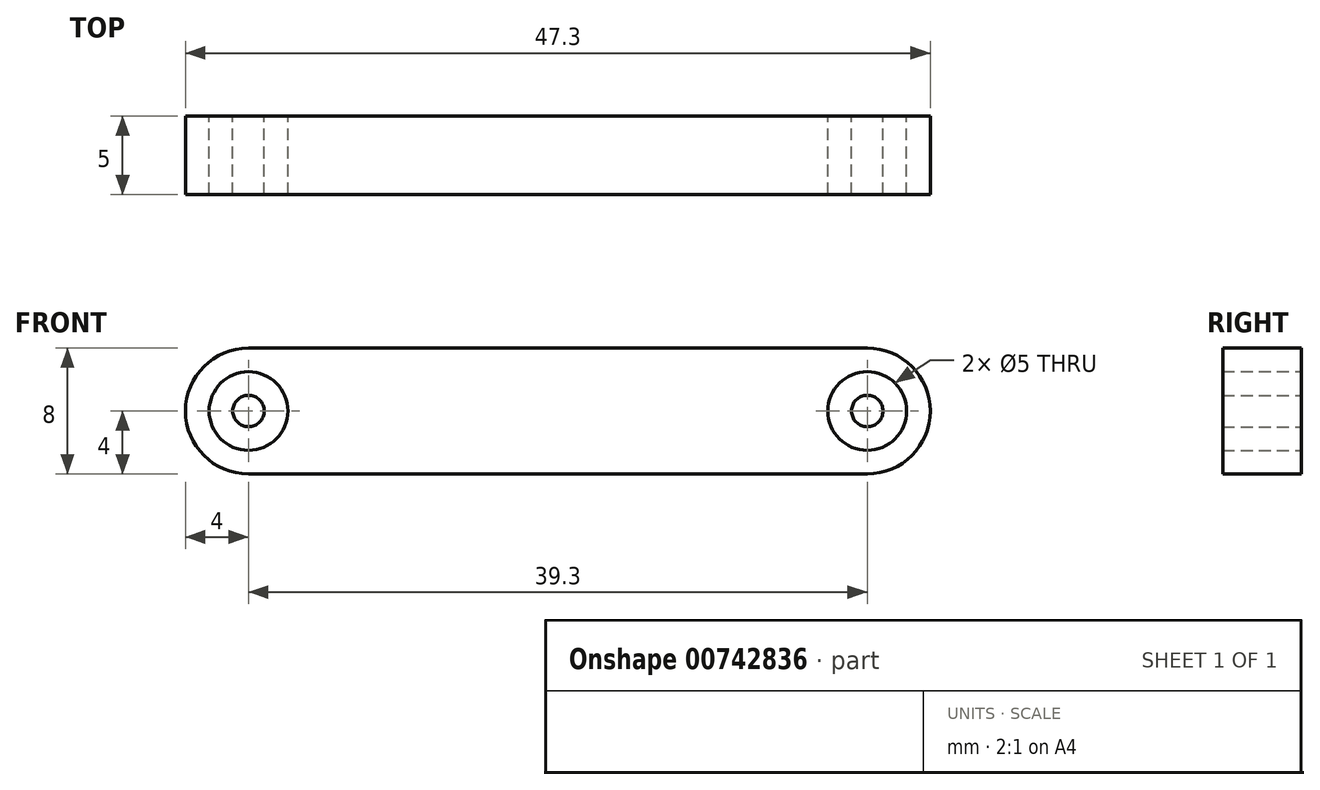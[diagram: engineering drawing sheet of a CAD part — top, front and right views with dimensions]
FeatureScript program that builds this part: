
annotation { "Feature Type Name" : "Feature", "Feature Type Description" : "" }
export const myFeature = defineFeature(function(context is Context, id is Id, definition is map)
    precondition{}
    {
        {
            var Q0;
            Q0=qCreatedBy(makeId("Front.planeOp"),FACE);
            var sketch = newSketch(context, id + "F0", { "sketchPlane" : qUnion([Q0])});
            skCircle(sketch, "E0", {"center": v(0, 0) * mm, "radius": 4 * mm});
            skCircle(sketch, "E1", {"center": v(39.3, 0) * mm, "radius": 4 * mm});
            skLineSegment(sketch, "E2", {"start": v(0, 4) * mm, "end": v(39.3, 4) * mm});
            skLineSegment(sketch, "E3", {"start": v(0, -4) * mm, "end": v(39.3, -4) * mm});
            skCircle(sketch, "E4", {"center": v(0, 0) * mm, "radius": 2.5 * mm});
            skCircle(sketch, "E5", {"center": v(39.3, 0) * mm, "radius": 2.5 * mm});
            skCircle(sketch, "E6", {"center": v(0, 0) * mm, "radius": 1 * mm});
            skCircle(sketch, "E7", {"center": v(39.3, 0) * mm, "radius": 1 * mm});
            skSolve(sketch);
        }
        {
            var Q0;
            Q0 = qSketchRegion(id + "F0", true);
            var Q1;
            Q1=makeQuery(id+"F0.imprint","IMPRINT",FACE,{"disambiguationData":[TD([[makeQuery(id+"F0.imprint","IMPRINT",EDGE,{"derivedFrom":sQuery(id+"F0.wireOp",EDGE,"E6")}),1.0]])]});
            var Q2;
            Q2=makeQuery(id+"F0.imprint","IMPRINT",FACE,{"disambiguationData":[TD([[makeQuery(id+"F0.imprint","IMPRINT",EDGE,{"derivedFrom":sQuery(id+"F0.wireOp",EDGE,"E7")}),1.0]])]});
            extrude(context, id + "F1", {"entities" : qUnion([Q0, Q1, Q2]), "depth" : 5 * mm, "offsetDistance" : 25 * mm});
        }
    });
